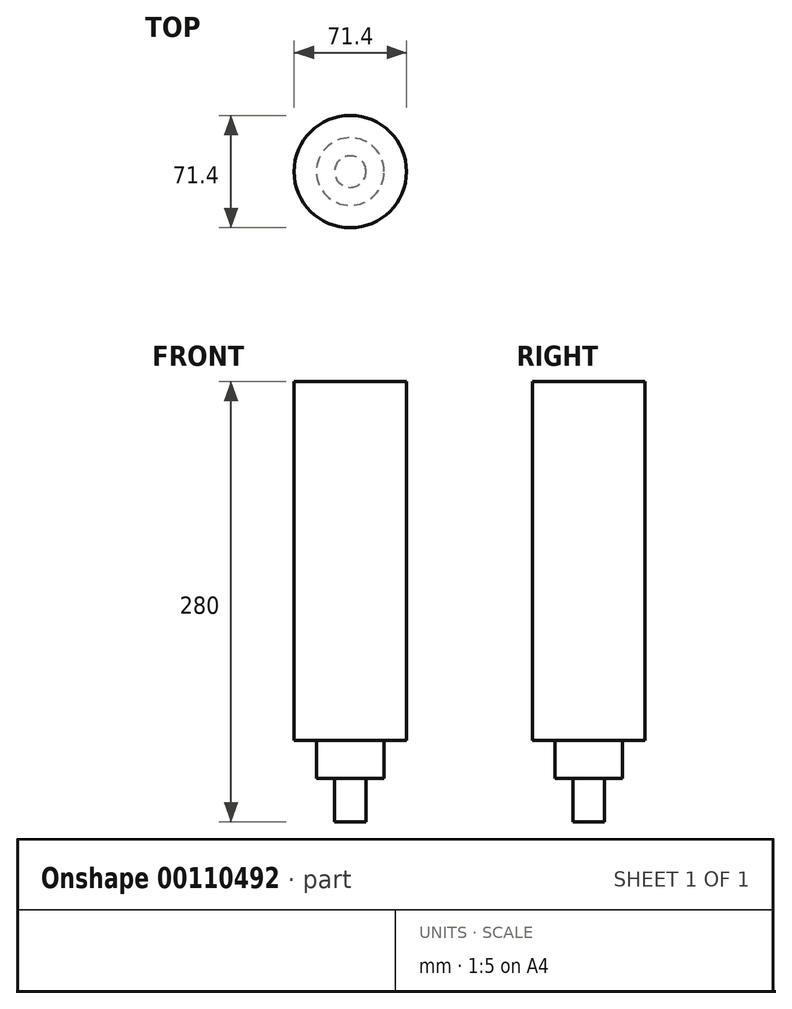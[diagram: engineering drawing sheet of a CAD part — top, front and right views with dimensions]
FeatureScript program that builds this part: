
annotation { "Feature Type Name" : "Feature", "Feature Type Description" : "" }
export const myFeature = defineFeature(function(context is Context, id is Id, definition is map)
    precondition{}
    {
        {
            var Q0;
            Q0=qCreatedBy(makeId("Front.planeOp"),FACE);
            var sketch = newSketch(context, id + "F0", { "sketchPlane" : qUnion([Q0])});
            skLineSegment(sketch, "E0.right", {"start": v(71.4, 0) * mm, "end": v(71.4, -228.2) * mm});
            skLineSegment(sketch, "E1.right", {"start": v(57.2, -228.2) * mm, "end": v(57.2, -252.2) * mm});
            skLineSegment(sketch, "E2.right", {"start": v(45.7, -252.2) * mm, "end": v(45.7, -280) * mm});
            skLineSegment(sketch, "E3", {"start": v(35.7, 0) * mm, "end": v(35.7, -280) * mm});
            skLineSegment(sketch, "E4", {"start": v(35.7, 0) * mm, "end": v(71.4, 0) * mm});
            skLineSegment(sketch, "E5", {"start": v(35.7, -280) * mm, "end": v(45.7, -280) * mm});
            skLineSegment(sketch, "E6", {"start": v(57.2, -228.2) * mm, "end": v(71.4, -228.2) * mm});
            skLineSegment(sketch, "E7", {"start": v(45.7, -252.2) * mm, "end": v(57.2, -252.2) * mm});
            skSolve(sketch);
        }
        {
            var Q0;
            Q0=makeQuery(id+"F0.imprint","IMPRINT",FACE,{"disambiguationData":[TD([[makeQuery(id+"F0.imprint","IMPRINT",EDGE,{"derivedFrom":sQuery(id+"F0.wireOp",EDGE,"E0.bottom")}),-1.0]])]});
            var Q1;
            Q1=makeQuery(id+"F0.imprint","IMPRINT",FACE,{"disambiguationData":[TD([[makeQuery(id+"F0.imprint","IMPRINT",EDGE,{"derivedFrom":sQuery(id+"F0.wireOp",EDGE,"E0.right")}),-1.0]])]});
            var Q2;
            Q2=sQuery(id+"F0.wireOp",EDGE,"E3");
            revolve(context, id + "F1", {"entities" : qUnion([Q0, Q1]), "axis" : qUnion([Q2]), "revolveType" : RevolveType.FULL});
        }
    });
